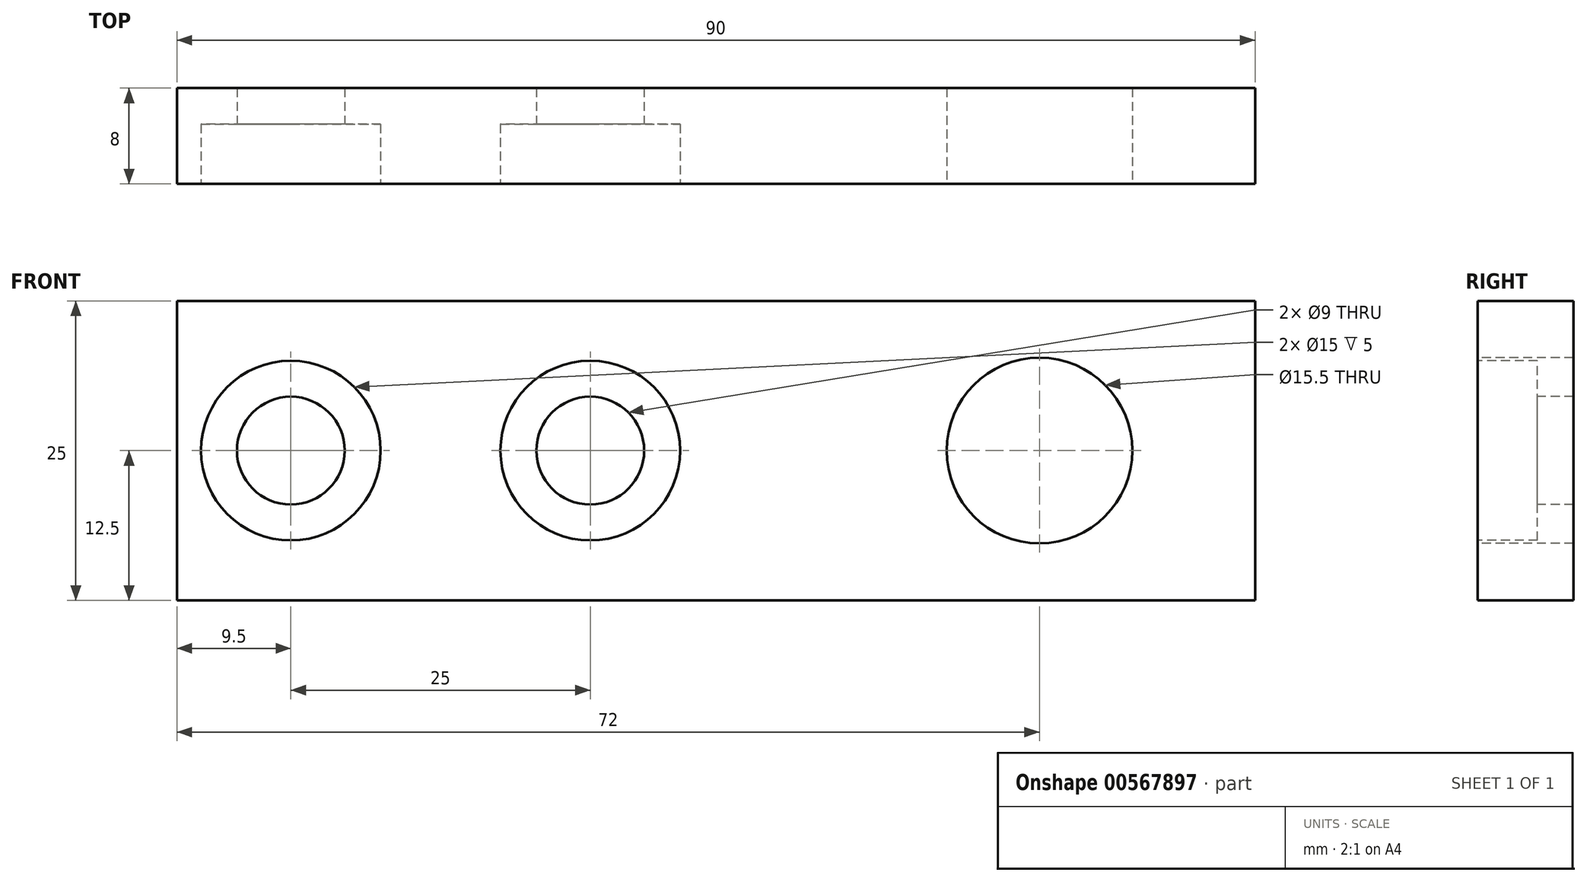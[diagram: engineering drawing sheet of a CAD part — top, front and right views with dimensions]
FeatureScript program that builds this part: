
annotation { "Feature Type Name" : "Feature", "Feature Type Description" : "" }
export const myFeature = defineFeature(function(context is Context, id is Id, definition is map)
    precondition{}
    {
        {
            var Q0;
            Q0=qCreatedBy(makeId("Front.planeOp"),FACE);
            var sketch = newSketch(context, id + "F0", { "sketchPlane" : qUnion([Q0])});
            skLineSegment(sketch, "E0.bottom", {"start": v(45, -12.5) * mm, "end": v(-45, -12.5) * mm});
            skLineSegment(sketch, "E0.top", {"start": v(45, 12.5) * mm, "end": v(-45, 12.5) * mm});
            skLineSegment(sketch, "E0.left", {"start": v(45, -12.5) * mm, "end": v(45, 12.5) * mm});
            skLineSegment(sketch, "E0.right", {"start": v(-45, -12.5) * mm, "end": v(-45, 12.5) * mm});
            skPoint(sketch, "E0.middle", {"position": v(0, 0) * mm});
            skSolve(sketch);
        }
        {
            var Q0;
            Q0 = qSketchRegion(id + "F0", true);
            extrude(context, id + "F1", {"entities" : qUnion([Q0]), "depth" : 8 * mm, "offsetDistance" : 25 * mm});
        }
        {
            var Q0;
            Q0=makeQuery(id+"F1.opExtrude","CAP_FACE",FACE,{"disambiguationData":[OSD([sQuery(id+"F0.wireOp",EDGE,"E0.bottom"),sQuery(id+"F0.wireOp",EDGE,"E0.top"),sQuery(id+"F0.wireOp",EDGE,"E0.left"),sQuery(id+"F0.wireOp",EDGE,"E0.right")])],"isStart":false});
            var sketch = newSketch(context, id + "F2", { "sketchPlane" : qUnion([Q0])});
            skCircle(sketch, "E1", {"center": v(-35.5, 0) * mm, "radius": 7.5 * mm});
            skPoint(sketch, "E1.centerSnap0", {"position": v(-45, 0) * mm});
            skCircle(sketch, "E2", {"center": v(-10.5, 0) * mm, "radius": 7.5 * mm});
            skCircle(sketch, "E3", {"center": v(27, 0) * mm, "radius": 7.75 * mm});
            skCircle(sketch, "E4", {"center": v(-35.5, 0) * mm, "radius": 4.5 * mm});
            skCircle(sketch, "E5", {"center": v(-10.5, 0) * mm, "radius": 4.5 * mm});
            skSolve(sketch);
        }
        {
            var Q0;
            Q0=makeQuery(id+"F2.imprint","IMPRINT",FACE,{"disambiguationData":[TD([[makeQuery(id+"F2.imprint","IMPRINT",EDGE,{"derivedFrom":sQuery(id+"F2.wireOp",EDGE,"E4")}),1.0]])]});
            var Q1;
            Q1=makeQuery(id+"F2.imprint","IMPRINT",FACE,{"disambiguationData":[TD([[makeQuery(id+"F2.imprint","IMPRINT",EDGE,{"derivedFrom":sQuery(id+"F2.wireOp",EDGE,"E5")}),1.0]])]});
            var Q2;
            Q2=makeQuery(id+"F2.imprint","IMPRINT",FACE,{"disambiguationData":[TD([[makeQuery(id+"F2.imprint","IMPRINT",EDGE,{"derivedFrom":sQuery(id+"F2.wireOp",EDGE,"E3")}),1.0]])]});
            extrude(context, id + "F3", {"entities" : qUnion([Q0, Q1, Q2]), "operationType" : NewBodyOperationType.REMOVE, "endBound" : BoundingType.UP_TO_NEXT, "oppositeDirection" : true, "depth" : 25 * mm, "offsetDistance" : 25 * mm});
        }
        {
            var Q0;
            Q0 = qSketchRegion(id + "F2", true);
            extrude(context, id + "F4", {"entities" : qUnion([Q0]), "operationType" : NewBodyOperationType.REMOVE, "oppositeDirection" : true, "depth" : 5 * mm, "offsetDistance" : 25 * mm});
        }
    });
